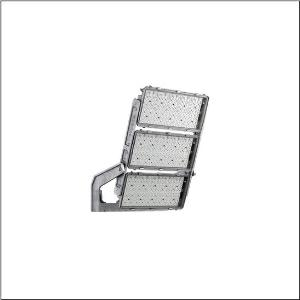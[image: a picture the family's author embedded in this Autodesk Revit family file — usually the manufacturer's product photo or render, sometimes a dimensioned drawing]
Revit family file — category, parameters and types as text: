
# Revit family: floodlight_fl_11_maxi_pro_remote___pl33t_5xa779428t01aa_0213
name_source: partatom
category: Lighting Fixtures
units: mm (PartAtom-declared; Revit-internal decimal feet)

## family parameters
Cut with Voids When Loaded = No
Host = Face
Light Source = No
Part Type = Normal
Room Calculation Point = No
Round Connector Dimension = Use Diameter
Shared = No

## types (1)
- --- (1 x LED, 191730 lm, 1539.6 W, 5700K)
    Apparent Load = 1540 VA
    CIE Flux Codes = 27 70 98 100 100
    Color Rendering = 80
    Color Temperature = 5700K
    Default Elevation = 1800 mm
    Description = Floodlight FL 11  maxi  pro Remote floodlight; light control with lens of PMMA; cover panel of toughened safety glass, transparent; light distribution: PL33T, asymmetric direct distribution, LEDcolour temperature: 5700K, rated luminous flux: 191.730lm, colour rendering: CRI > 80, light colour: 857; luminous efficacy: 125lm/W; brightness control: DALI 2 (1 DALI address); with terminal, 8-pole, max. 2.5mm², mains connection: 220..240V/380..400V AC, 50/60Hz, surge voltage resistance: line to ground: 10kV, dimming range 10..100%, dustproof LED module, LED unit replaceable without ESD environment, no afterglow with DALI off / DMX off command, ECG replaceable separately; 1540W floodlight with 3x LED unit of diecast aluminium, coated grey; length: 1.003mm / width: 651mm / height: 338mm; mounting bracket, of diecast aluminium, uncoated, natural, equipment: Power, protection rating (complete): IP66; insulation class (complete): insulation class I (protective earthing); certification: CE, ENEC, VDE; ball protection: ball impact resistant, impact resistance: IK07; only for outdoor installations, rated ambient temperature 10°C, permissible operating ambient temperature: -40..+30°C, permissible storage temperature: -40..+85°C; packaging unit: 1 piece

Light Distribution: PL33T
    Height = 320 mm
    Lamp = 1 x LED
    Lamp Light Flux = 191730 lm
    Lamp Power = 1539.6 W
    Lamp count = 1
    Length = 1002 mm
    Luminous efficacy = 125 lm/W
    Manufacturer = Siteco
    ModVariant = No
    Model = 5XA779428T01AA
    Mounting Place = Ceiling
    Mounting Type = Surface mounted
    Number of Poles = 1
    OnlyDefault = Yes
    Power Factor = 1
    Product Name = Floodlight FL 11 maxi pro Remote | PL33T
    Product group = floodlight | ceiling mounted
    ProductGroupID = 302
    Protection Class = Protection class I
    Protection Degree = IP 66
    RLX_Detail_Level = 1
    RLX_Emergency_Light_Flux = 0 lm
    RLX_Emergency_Type = 0
    RLX_Emergency_Type_DB = No
    RlxData = <blob elided: 52449 chars, md5=6c9618e1>
    Socket = socket
    Standby Power = 0 W
    System Light Flux = 191730 lm
    System Power = 1540 W
    Type Comments = factory setting: luminous flux: 100 % | dim-lin: 254 | 1080 mA
    Type Image = l_1006784.jpg
    URL = http://relux.com
    VarID = @adj_048023
    Voltage = 0 V
    Weight = 0.00 kg
    Width = 655 mm

## geometry (parser evidence)
native form markers: Blend x4, Sweep x13
no freeform markers — native parametric forms only
